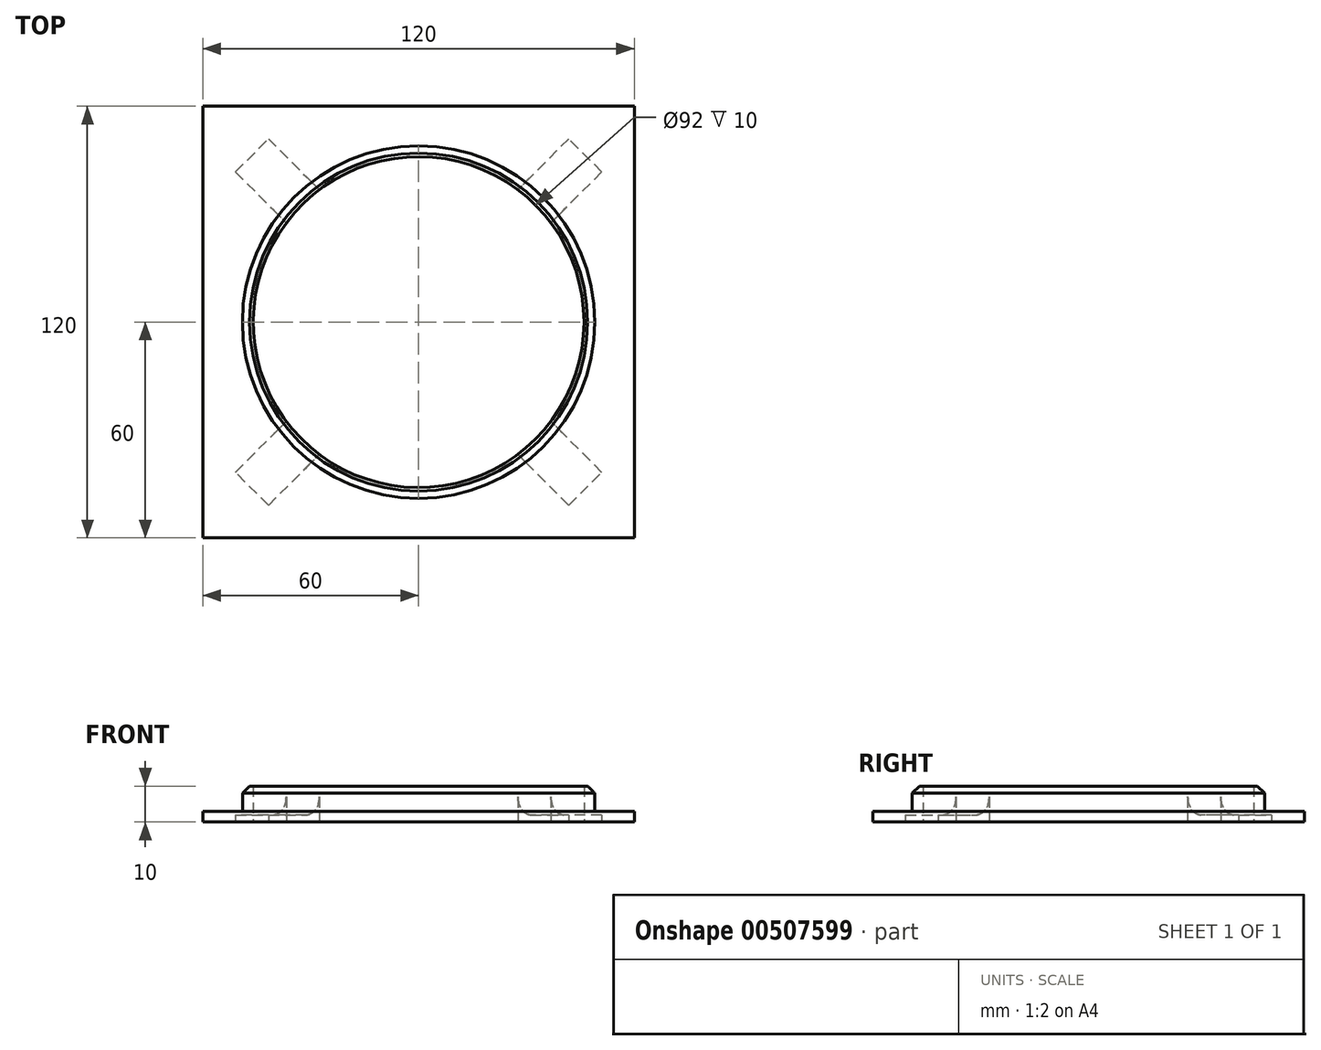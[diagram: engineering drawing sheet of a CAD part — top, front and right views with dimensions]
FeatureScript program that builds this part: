
annotation { "Feature Type Name" : "Feature", "Feature Type Description" : "" }
export const myFeature = defineFeature(function(context is Context, id is Id, definition is map)
    precondition{}
    {
        {
            var Q0;
            Q0=qCreatedBy(makeId("Top.planeOp"),FACE);
            var sketch = newSketch(context, id + "F0", { "sketchPlane" : qUnion([Q0])});
            skLineSegment(sketch, "E0.bottom", {"start": v(60, -60) * mm, "end": v(-60, -60) * mm});
            skLineSegment(sketch, "E0.top", {"start": v(60, 60) * mm, "end": v(-60, 60) * mm});
            skLineSegment(sketch, "E0.left", {"start": v(60, -60) * mm, "end": v(60, 60) * mm});
            skLineSegment(sketch, "E0.right", {"start": v(-60, -60) * mm, "end": v(-60, 60) * mm});
            skPoint(sketch, "E0.middle", {"position": v(0, 0) * mm});
            skCircle(sketch, "E1", {"center": v(0, 0) * mm, "radius": 46 * mm});
            skCircle(sketch, "E2", {"center": v(0, 0) * mm, "radius": 49 * mm});
            skSolve(sketch);
        }
        {
            var Q0;
            Q0=makeQuery(id+"F0.imprint","IMPRINT",FACE,{"disambiguationData":[TD([[makeQuery(id+"F0.imprint","IMPRINT",EDGE,{"derivedFrom":sQuery(id+"F0.wireOp",EDGE,"E1")}),-1.0]])]});
            extrude(context, id + "F1", {"entities" : qUnion([Q0]), "depth" : 10 * mm});
        }
        {
            var Q0;
            Q0=makeQuery(id+"F0.imprint","IMPRINT",FACE,{"disambiguationData":[TD([[makeQuery(id+"F0.imprint","IMPRINT",EDGE,{"derivedFrom":sQuery(id+"F0.wireOp",EDGE,"E0.bottom")}),-1.0]])]});
            extrude(context, id + "F2", {"entities" : qUnion([Q0]), "operationType" : NewBodyOperationType.ADD, "depth" : 3 * mm});
        }
        {
            var Q0;
            Q0=makeQuery(id+"F1.opExtrude","CAP_EDGE",EDGE,{"disambiguationData":[OSD([sQuery(id+"F0.wireOp",EDGE,"E2")])],"isStart":false});
            chamfer(context, id + "F3", {"entities" : qUnion([Q0]), "width" : 2 * mm, "tangentPropagation" : true});
        }
        {
            var Q0;
            {var subQ0=sQuery(id+"F0.wireOp",EDGE,"E2");Q0=makeQuery(id+"F2.boolean.opBoolean","MERGE",FACE,{"derivedFrom":[makeQuery(id+"F1.opExtrude","CAP_FACE",FACE,{"disambiguationData":[OSD([sQuery(id+"F0.wireOp",EDGE,"E1"),subQ0])],"isStart":true}),makeQuery(id+"F2.opExtrude","CAP_FACE",FACE,{"disambiguationData":[OSD([sQuery(id+"F0.wireOp",EDGE,"E0.bottom"),sQuery(id+"F0.wireOp",EDGE,"E0.top"),sQuery(id+"F0.wireOp",EDGE,"E0.left"),sQuery(id+"F0.wireOp",EDGE,"E0.right"),subQ0])],"isStart":true})]});}
            var sketch = newSketch(context, id + "F4", { "sketchPlane" : qUnion([Q0])});
            skLineSegment(sketch, "E3", {"start": v(-60, 60) * mm, "end": v(60, -60) * mm, "construction": true});
            skLineSegment(sketch, "E4", {"start": v(60, 60) * mm, "end": v(-60, -60) * mm, "construction": true});
            skLineSegment(sketch, "E5", {"start": v(-41.75, 50.94) * mm, "end": v(-50.94, 41.75) * mm});
            skLineSegment(sketch, "E6.MirrorCS", {"start": v(50.94, -41.75) * mm, "end": v(41.75, -50.94) * mm});
            skLineSegment(sketch, "E7", {"start": v(-41.75, 50.94) * mm, "end": v(-27.6, 36.8) * mm});
            skLineSegment(sketch, "E8", {"start": v(-27.6, 36.8) * mm, "end": v(-36.8, 27.6) * mm});
            skLineSegment(sketch, "E9.MirrorCS", {"start": v(41.75, 50.94) * mm, "end": v(27.6, 36.8) * mm});
            skLineSegment(sketch, "E10.MirrorCS", {"start": v(41.75, 50.94) * mm, "end": v(50.94, 41.75) * mm});
            skLineSegment(sketch, "E11.MirrorCS", {"start": v(27.6, 36.8) * mm, "end": v(36.8, 27.6) * mm});
            skLineSegment(sketch, "E12.MirrorCS", {"start": v(50.94, -41.75) * mm, "end": v(36.8, -27.6) * mm});
            skLineSegment(sketch, "E13.MirrorCS", {"start": v(36.8, -27.6) * mm, "end": v(27.6, -36.8) * mm});
            skLineSegment(sketch, "E14.MirrorCS", {"start": v(-50.94, 41.75) * mm, "end": v(-36.8, 27.6) * mm});
            skLineSegment(sketch, "E15.MirrorCS", {"start": v(41.75, -50.94) * mm, "end": v(27.6, -36.8) * mm});
            skLineSegment(sketch, "E16.MirrorCS", {"start": v(-50.94, -41.75) * mm, "end": v(-36.8, -27.6) * mm});
            skLineSegment(sketch, "E17.MirrorCS", {"start": v(-50.94, -41.75) * mm, "end": v(-41.75, -50.94) * mm});
            skLineSegment(sketch, "E18.MirrorCS", {"start": v(-36.8, -27.6) * mm, "end": v(-27.6, -36.8) * mm});
            skLineSegment(sketch, "E19.MirrorCS", {"start": v(50.94, 41.75) * mm, "end": v(36.8, 27.6) * mm});
            skLineSegment(sketch, "E20.MirrorCS", {"start": v(60, -60) * mm, "end": v(-60, 60) * mm, "construction": true});
            skLineSegment(sketch, "E21.MirrorCS", {"start": v(-41.75, -50.94) * mm, "end": v(-27.6, -36.8) * mm});
            skSolve(sketch);
        }
        {
            var Q0;
            Q0 = qSketchRegion(id + "F4", true);
            extrude(context, id + "F5", {"entities" : qUnion([Q0]), "operationType" : NewBodyOperationType.REMOVE, "oppositeDirection" : true, "depth" : 2 * mm});
        }
        {
            var Q0;
            Q0=makeQuery(id+"F5.boolean.opBoolean","INTERSECT",EDGE,{"derivedFrom":[makeQuery(id+"F1.opExtrude","SWEPT_FACE",FACE,{"disambiguationData":[OSD([sQuery(id+"F0.wireOp",EDGE,"E1")])]}),makeQuery(id+"F5.opExtrude","CAP_FACE",FACE,{"disambiguationData":[OSD([sQuery(id+"F4.wireOp",EDGE,"E5"),sQuery(id+"F4.wireOp",EDGE,"E7"),sQuery(id+"F4.wireOp",EDGE,"E8"),sQuery(id+"F4.wireOp",EDGE,"E14.MirrorCS")])],"isStart":false})]});
            var Q1;
            Q1=makeQuery(id+"F5.boolean.opBoolean","INTERSECT",EDGE,{"derivedFrom":[makeQuery(id+"F1.opExtrude","SWEPT_FACE",FACE,{"disambiguationData":[OSD([sQuery(id+"F0.wireOp",EDGE,"E1")])]}),makeQuery(id+"F5.opExtrude","CAP_FACE",FACE,{"disambiguationData":[OSD([sQuery(id+"F4.wireOp",EDGE,"E10.MirrorCS"),sQuery(id+"F4.wireOp",EDGE,"E11.MirrorCS"),sQuery(id+"F4.wireOp",EDGE,"E19.MirrorCS"),sQuery(id+"F4.wireOp",EDGE,"E9.MirrorCS")])],"isStart":false})]});
            var Q2;
            Q2=makeQuery(id+"F5.boolean.opBoolean","INTERSECT",EDGE,{"derivedFrom":[makeQuery(id+"F1.opExtrude","SWEPT_FACE",FACE,{"disambiguationData":[OSD([sQuery(id+"F0.wireOp",EDGE,"E1")])]}),makeQuery(id+"F5.opExtrude","CAP_FACE",FACE,{"disambiguationData":[OSD([sQuery(id+"F4.wireOp",EDGE,"E6.MirrorCS"),sQuery(id+"F4.wireOp",EDGE,"E12.MirrorCS"),sQuery(id+"F4.wireOp",EDGE,"E13.MirrorCS"),sQuery(id+"F4.wireOp",EDGE,"E15.MirrorCS")])],"isStart":false})]});
            var Q3;
            Q3=makeQuery(id+"F5.boolean.opBoolean","INTERSECT",EDGE,{"derivedFrom":[makeQuery(id+"F1.opExtrude","SWEPT_FACE",FACE,{"disambiguationData":[OSD([sQuery(id+"F0.wireOp",EDGE,"E1")])]}),makeQuery(id+"F5.opExtrude","CAP_FACE",FACE,{"disambiguationData":[OSD([sQuery(id+"F4.wireOp",EDGE,"E16.MirrorCS"),sQuery(id+"F4.wireOp",EDGE,"E17.MirrorCS"),sQuery(id+"F4.wireOp",EDGE,"E18.MirrorCS"),sQuery(id+"F4.wireOp",EDGE,"E21.MirrorCS")])],"isStart":false})]});
            fillet(context, id + "F6", {"entities" : qUnion([Q0, Q1, Q2, Q3]), "radius" : 5 * mm, "tangentPropagation" : true, "allowEdgeOverflow" : false});
        }
    });
